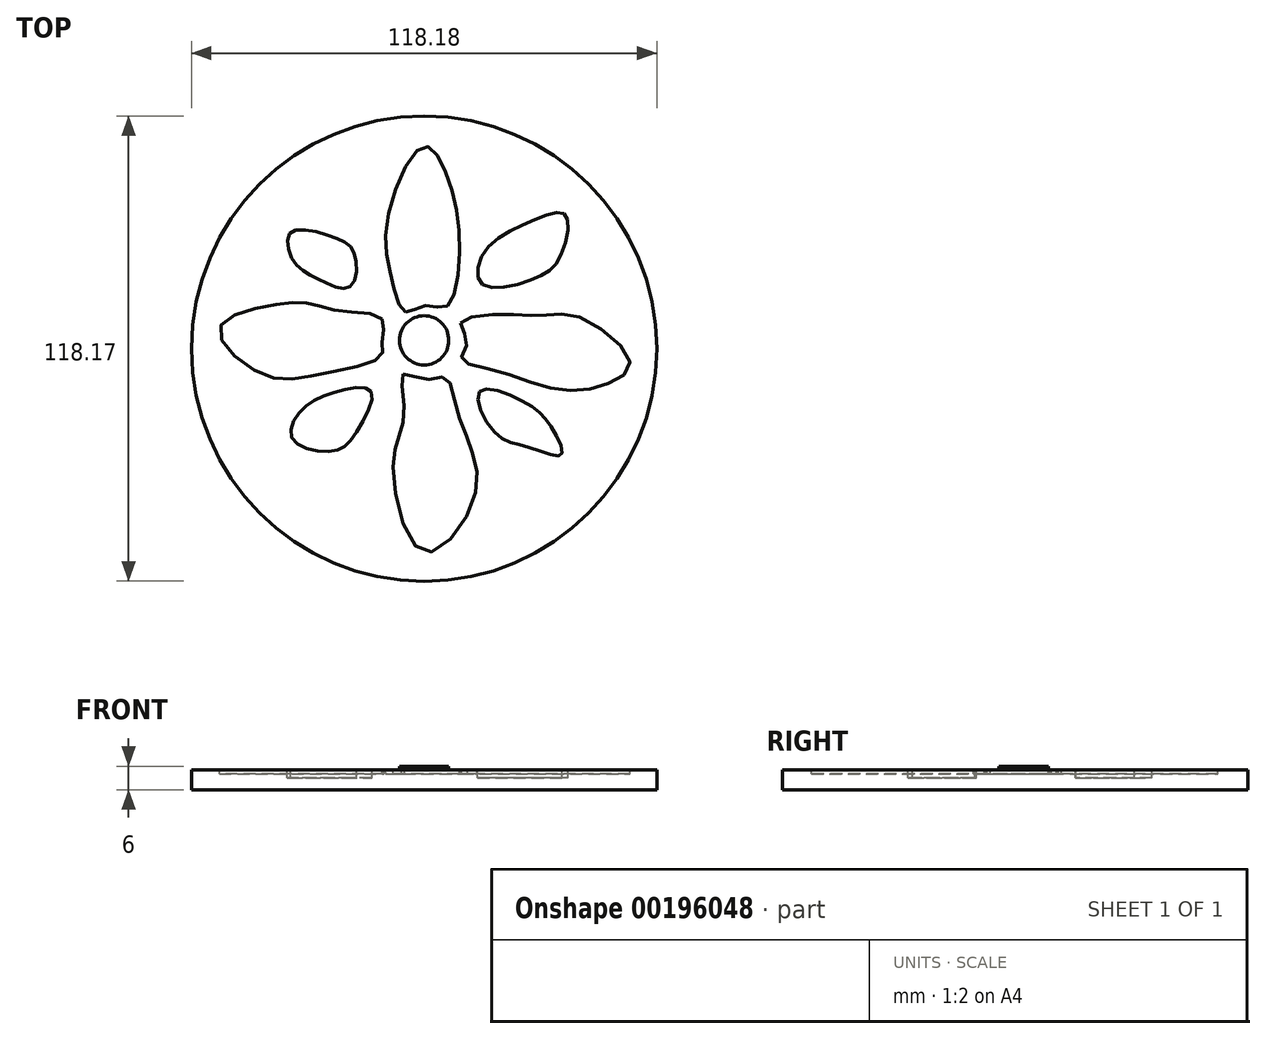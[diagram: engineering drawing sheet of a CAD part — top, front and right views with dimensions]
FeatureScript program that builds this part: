
annotation { "Feature Type Name" : "Feature", "Feature Type Description" : "" }
export const myFeature = defineFeature(function(context is Context, id is Id, definition is map)
    precondition{}
    {
        {
            var Q0;
            Q0=qCreatedBy(makeId("Top.planeOp"),FACE);
            var sketch = newSketch(context, id + "F0", { "sketchPlane" : qUnion([Q0])});
            skCircle(sketch, "E0", {"center": v(0, -2.1) * mm, "radius": 59.09 * mm});
            skSolve(sketch);
        }
        {
            var Q0;
            Q0=makeQuery(id+"F0.imprint","IMPRINT",FACE,{"disambiguationData":[TD([[makeQuery(id+"F0.imprint","IMPRINT",EDGE,{"derivedFrom":sQuery(id+"F0.wireOp",EDGE,"E0")}),1.0]])]});
            extrude(context, id + "F1", {"entities" : qUnion([Q0]), "depth" : 5 * mm});
        }
        {
            var Q0;
            Q0=makeQuery(id+"F1.opExtrude","CAP_FACE",FACE,{"disambiguationData":[OSD([sQuery(id+"F0.wireOp",EDGE,"E0")])],"isStart":false});
            var sketch = newSketch(context, id + "F2", { "sketchPlane" : qUnion([Q0])});
            skCircle(sketch, "E1", {"center": v(0, 0) * mm, "radius": 6.25 * mm});
            skSolve(sketch);
        }
        {
            var Q0;
            Q0=makeQuery(id+"F2.imprint","IMPRINT",FACE,{"disambiguationData":[TD([[makeQuery(id+"F2.imprint","IMPRINT",EDGE,{"derivedFrom":sQuery(id+"F2.wireOp",EDGE,"E1")}),-1.0]])]});
            var sketch = newSketch(context, id + "F3", { "sketchPlane" : qUnion([Q0])});
            skFitSpline(sketch, "E2", {"points": [v(-4.77, 7.16) * mm, v(-8.14, 15.3) * mm, v(-9.26, 31.3) * mm, v(0, 49.27) * mm, v(5.9, 41.7) * mm, v(8.98, 22.88) * mm, v(5.61, 8.56) * mm, v(0, 8.84) * mm, v(-4.77, 7.16) * mm]});
            skFitSpline(sketch, "E3", {"points": [v(9.26, 4.35) * mm, v(10.95, 0) * mm, v(9.55, -4.63) * mm, v(18.25, -7.72) * mm, v(33.97, -12.5) * mm, v(46.6, -11.09) * mm, v(52.22, -5.47) * mm, v(39.02, 6.04) * mm, v(30.04, 6.32) * mm, v(19.37, 6.6) * mm, v(9.26, 4.35) * mm]});
            skFitSpline(sketch, "E4", {"points": [v(-5.33, -8.56) * mm, v(0, -9.97) * mm, v(5.33, -9.4) * mm, v(8.14, -16.99) * mm, v(12.07, -27.93) * mm, v(12.35, -41.13) * mm, v(0, -53.76) * mm, v(-7.86, -33.55) * mm, v(-6.46, -24.57) * mm, v(-5.05, -16.99) * mm, v(-5.33, -8.56) * mm]});
            skFitSpline(sketch, "E5", {"points": [v(-10.67, 5.47) * mm, v(-21.06, 7.44) * mm, v(-29.48, 9.4) * mm, v(-39.3, 8.84) * mm, v(-51.94, 2.95) * mm, v(-41.27, -8.56) * mm, v(-26.4, -8.56) * mm, v(-10.95, -4.07) * mm, v(-10.67, 0) * mm, v(-10.67, 5.47) * mm]});
            skFitSpline(sketch, "E6", {"points": [v(15.16, 18.39) * mm, v(19.37, 12.77) * mm, v(39.59, 14.74) * mm, v(41.27, 23.44) * mm, v(15.16, 18.39) * mm]});
            skFitSpline(sketch, "E7", {"points": [v(-17.69, 18.39) * mm, v(-24.14, 26.25) * mm, v(-37.06, 26.53) * mm, v(-33.97, 18.39) * mm, v(-17.69, 18.39) * mm]});
            skFitSpline(sketch, "E8", {"points": [v(-14.04, -14.46) * mm, v(-22.18, -15.3) * mm, v(-28.36, -24.57) * mm, v(-28.92, -31.58) * mm, v(-18.53, -29.62) * mm, v(-13.76, -23.44) * mm, v(-14.04, -14.46) * mm]});
            skFitSpline(sketch, "E9", {"points": [v(15.16, -14.74) * mm, v(17.69, -22.32) * mm, v(23.86, -27.93) * mm, v(30.04, -29.9) * mm, v(29.2, -24.28) * mm, v(27.23, -18.1) * mm, v(15.16, -14.74) * mm]});
            skSolve(sketch);
        }
        {
            var Q0;
            Q0=makeQuery(id+"F2.imprint","IMPRINT",FACE,{"disambiguationData":[TD([[makeQuery(id+"F2.imprint","IMPRINT",EDGE,{"derivedFrom":sQuery(id+"F2.wireOp",EDGE,"E1")}),1.0]])]});
            extrude(context, id + "F4", {"entities" : qUnion([Q0]), "operationType" : NewBodyOperationType.ADD, "depth" : 1 * mm});
        }
        {
            var Q0;
            Q0=makeQuery(id+"F3.imprint","IMPRINT",FACE,{"disambiguationData":[TD([[makeQuery(id+"F3.imprint","IMPRINT",EDGE,{"derivedFrom":sQuery(id+"F3.wireOp",EDGE,"E2")}),-1.0]])]});
            var Q1;
            Q1=makeQuery(id+"F3.imprint","IMPRINT",FACE,{"disambiguationData":[TD([[makeQuery(id+"F3.imprint","IMPRINT",EDGE,{"derivedFrom":sQuery(id+"F3.wireOp",EDGE,"E5")}),1.0]])]});
            var Q2;
            Q2=makeQuery(id+"F3.imprint","IMPRINT",FACE,{"disambiguationData":[TD([[makeQuery(id+"F3.imprint","IMPRINT",EDGE,{"derivedFrom":sQuery(id+"F3.wireOp",EDGE,"E4")}),-1.0]])]});
            var Q3;
            Q3=makeQuery(id+"F3.imprint","IMPRINT",FACE,{"disambiguationData":[TD([[makeQuery(id+"F3.imprint","IMPRINT",EDGE,{"derivedFrom":sQuery(id+"F3.wireOp",EDGE,"E3")}),1.0]])]});
            extrude(context, id + "F5", {"entities" : qUnion([Q0, Q1, Q2, Q3]), "operationType" : NewBodyOperationType.REMOVE, "oppositeDirection" : true, "depth" : 1 * mm});
        }
        {
            var Q0;
            Q0=makeQuery(id+"F1.opExtrude","CAP_FACE",FACE,{"disambiguationData":[OSD([sQuery(id+"F0.wireOp",EDGE,"E0")])],"isStart":false});
            var sketch = newSketch(context, id + "F6", { "sketchPlane" : qUnion([Q0])});
            skFitSpline(sketch, "E10", {"points": [v(-18.81, 13.62) * mm, v(-26.4, 15.3) * mm, v(-33.13, 20.07) * mm, v(-33.97, 27.37) * mm, v(-23.02, 26.25) * mm, v(-17.69, 22.04) * mm, v(-18.81, 13.62) * mm]});
            skFitSpline(sketch, "E11", {"points": [v(14.88, 14.18) * mm, v(15.16, 22.32) * mm, v(28.36, 30.74) * mm, v(35.94, 31.86) * mm, v(34.53, 21.2) * mm, v(27.8, 15.58) * mm, v(14.88, 14.18) * mm]});
            skFitSpline(sketch, "E12", {"points": [v(-13.48, -13.05) * mm, v(-22.18, -13.05) * mm, v(-31.44, -18.1) * mm, v(-33.4, -25.13) * mm, v(-23.58, -28.22) * mm, v(-17.69, -24) * mm, v(-13.48, -13.05) * mm]});
            skFitSpline(sketch, "E13", {"points": [v(14.04, -13.05) * mm, v(18.25, -23.72) * mm, v(26.4, -27.1) * mm, v(34.81, -29.06) * mm, v(32.29, -22.04) * mm, v(25.83, -15.86) * mm, v(14.04, -13.05) * mm]});
            skSolve(sketch);
        }
        {
            var Q0;
            Q0=makeQuery(id+"F6.imprint","IMPRINT",FACE,{"disambiguationData":[TD([[makeQuery(id+"F6.imprint","IMPRINT",EDGE,{"derivedFrom":sQuery(id+"F6.wireOp",EDGE,"E10")}),-1.0]])]});
            var Q1;
            Q1=makeQuery(id+"F6.imprint","IMPRINT",FACE,{"disambiguationData":[TD([[makeQuery(id+"F6.imprint","IMPRINT",EDGE,{"derivedFrom":sQuery(id+"F6.wireOp",EDGE,"E12")}),1.0]])]});
            var Q2;
            Q2=makeQuery(id+"F6.imprint","IMPRINT",FACE,{"disambiguationData":[TD([[makeQuery(id+"F6.imprint","IMPRINT",EDGE,{"derivedFrom":sQuery(id+"F6.wireOp",EDGE,"E13")}),1.0]])]});
            var Q3;
            Q3=makeQuery(id+"F6.imprint","IMPRINT",FACE,{"disambiguationData":[TD([[makeQuery(id+"F6.imprint","IMPRINT",EDGE,{"derivedFrom":sQuery(id+"F6.wireOp",EDGE,"E11")}),-1.0]])]});
            extrude(context, id + "F7", {"entities" : qUnion([Q0, Q1, Q2, Q3]), "operationType" : NewBodyOperationType.REMOVE, "oppositeDirection" : true, "depth" : 2 * mm});
        }
    });
